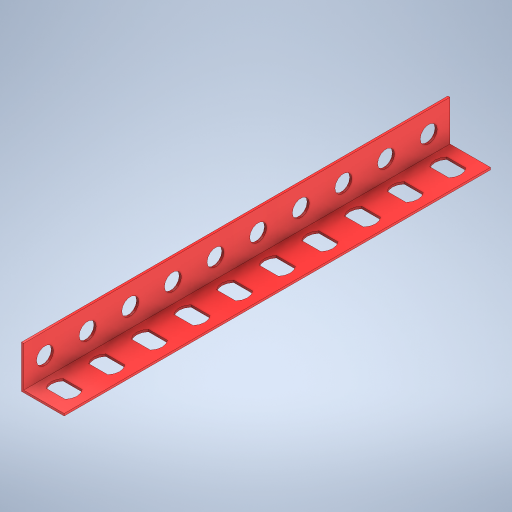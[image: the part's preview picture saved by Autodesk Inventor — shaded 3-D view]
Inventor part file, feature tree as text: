
AUTODESK INVENTOR PART (.ipt)
format: ipt  version: 2024 (Build 280153000, 153)  size: 344,064 bytes
history: native  units: mm
features: extrude x4, sketch x4, pattern_linear x2, other x1
ambient origin geometry x8: Origin, YZ Plane, XZ Plane, XY Plane, X Axis, Y Axis, Z Axis, Center Point
bodies: Body1 (feature_tree)
feature tree (11):
  other  "Těleso1"
  extrude  "Vysunutí1"  Depth=0.5mm
  extrude  "Vysunutí2"  Depth=0.5mm
  pattern_linear  "Obdélníkové pole1"  Spacing1=10.0mm  [1 undecoded]
  extrude  "Vysunutí4"  Depth=10.0mm
  extrude  "Vysunutí5"  Depth=100.0mm TaperAngle=0.0deg
  pattern_linear  "Obdélníkové pole3"  Spacing1=6.0mm  [1 undecoded]
  sketch  "Náčrt1"
  sketch  "Náčrt2"
  sketch  "Náčrt4"
  sketch  "Náčrt5"
note: 2 required parameter values undecoded (feature->parameter linkage not recoverable at this tier; creation-order binding heuristic only, values carry confidence <= 0.55)
